# Revit family: Lighting_Emergency&Security_Linergy_Spy-control
name_source: partatom
category: Electrical Fixtures
revit_build: Autodesk Revit 2018 (Build: 20190510_1515(x64)
units: mm (PartAtom-declared; Revit-internal decimal feet)

## family parameters
Always vertical = Yes
Cut with Voids When Loaded = No
Maintain Annotation Orientation = No
OmniClass Number = 23.35.31.00
OmniClass Title = Electrical Power Distribution Devices
Part Type = Normal
Room Calculation Point = No
Round Connector Dimension = Use Diameter
Shared = No
Work Plane-Based = No

## types (1)
- Lighting_Emergency&Security_Linergy_Spy-control
    Active power = 1000 W
    Apparent Load Phase 1 = 0 VA
    Apparent Load Phase 2 = 0 VA
    Apparent Load Phase 3 = 0 VA
    BIMobject category = Emergency & Security
    Battery = 3 x Pb 12 V
    Description = Central power systems with control, for emergency installations with self-contained and central battery luminaires.
    Design country = Italy
    Duration = 1 h
    Edition number = 1
    IFC Classification = Electric Distribution
    Installation = Floor
    Installation instructions = https://www.linergy.it
    Insulation class = I
    Main material = Linergy - Metal - Steel Powder-coated Black RAL 9005
    Main material texture = Linergy - Metal - Steel Powder-coated Black RAL 9005 texture 2
    Manufacturer = Linergy
    Manufacturer country = Italy
    Manufacturer name = Linergy
    Material main = Electrogalvanized
    Material secondary = Electronic & optical components
    Model = SC1801
    Nominal Power = 1000 VA
    Number of Poles = 1
    OmniClass Code = 23-35 31 00
    OmniClass Description = Electrical Power Distribution Devices
    Output circuits = 3 (NM/M)
    Output voltage = 230 Vac
    Power = 800 W
    Power supply = 230 Vac
    Product Guid = b7d6e35e-f043-4996-a94b-c3f62f6cd469
    Product SKU = spy-control
    Product certification = https://www.linergy.it
    Product data url = https://bimobject.com
    Product family = Centralized systems
    Product group = Centralized power supply (CPS) and control
    Product name = SPY CONTROL - Centralized system
    Product url = https://www.linergy.it
    QR code = https://bimobject.com
    SC1801_bottom part = Yes
    SC1801_upper part = Yes
    SC1803_bottom part = No
    SC1805_upper part = No
    SC1806 = No
    SC1807 = No
    SC1810_upper part = No
    SC1811 = No
    Screen material = Linergy - Plastic - Polycarbonate Transparent high polished
    Secondary material = Linergy - Plastic - Nylon Black
    Technical description = https://www.linergy.it
    URL = https://www.linergy.it
    URL - Article page = https://www.linergy.it
    Voltage = 230 V
    Wheels material = Linergy - Plastic - Nylon Black
    z_MEP loction = 198 mm
    z_upper unit location = 400 mm  [stored 1.31234 ft]
    z_upper unit location SC1811 = 860 mm
    z_upper unit location Y = 0 mm  [stored 0 ft]

note: [stored X ft] marks values corroborated as IEEE doubles in the binary element streams (Revit-internal decimal feet)

## geometry (parser evidence)
native form markers: Sweep x25
no freeform markers — native parametric forms only
